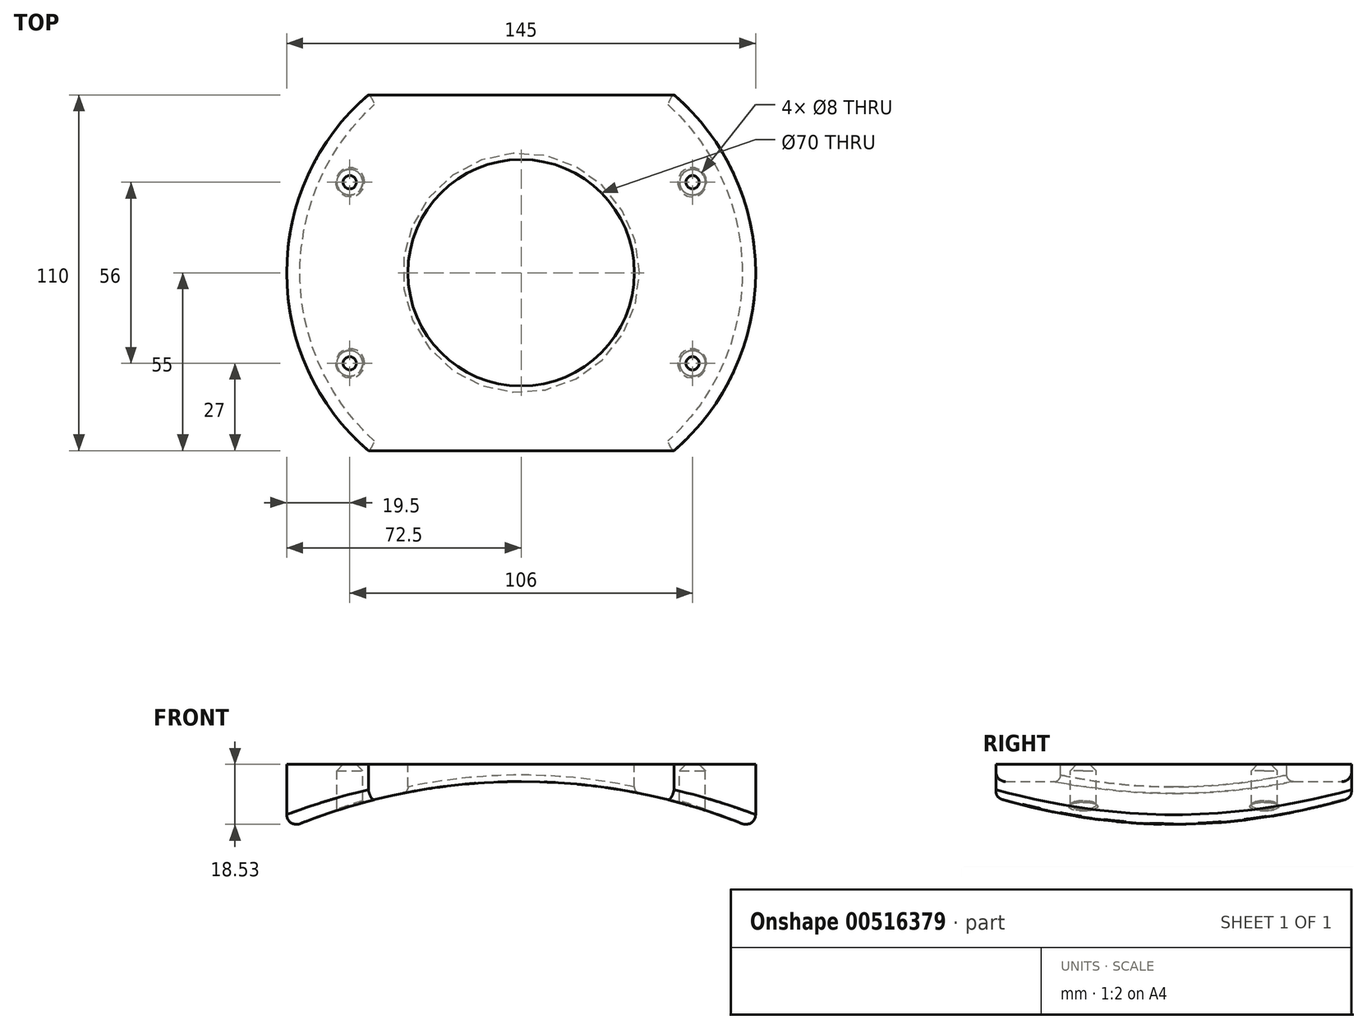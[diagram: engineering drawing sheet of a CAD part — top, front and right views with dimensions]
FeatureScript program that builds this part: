
annotation { "Feature Type Name" : "Feature", "Feature Type Description" : "" }
export const myFeature = defineFeature(function(context is Context, id is Id, definition is map)
    precondition{}
    {
        {
            var Q0;
            Q0=qCreatedBy(makeId("Front.planeOp"),FACE);
            var sketch = newSketch(context, id + "F0", { "sketchPlane" : qUnion([Q0])});
            skLineSegment(sketch, "E0.bottom", {"start": v(0, 0) * mm, "end": v(145, 0) * mm});
            skLineSegment(sketch, "E0.left", {"start": v(0, -20) * mm, "end": v(0, 0) * mm});
            skLineSegment(sketch, "E0.right", {"start": v(145, -20) * mm, "end": v(145, 0) * mm});
            skArc(sketch, "E1", {"start": v(145, -20) * mm, "mid": v(72.5, -5.29) * mm, "end": v(0, -20) * mm});
            skSolve(sketch);
        }
        {
            var Q0;
            Q0 = qSketchRegion(id + "F0", true);
            var Q1;
            Q1 = qSketchRegion(id + "F2", true);
            extrude(context, id + "F1", {"entities" : qUnion([Q0, Q1]), "depth" : 110 * mm, "offsetDistance" : 25 * mm});
        }
        {
            var Q0;
            Q0=makeQuery(id+"F1.opExtrude","SWEPT_FACE",FACE,{"disambiguationData":[OSD([sQuery(id+"F0.wireOp",EDGE,"E0.bottom")])]});
            var sketch = newSketch(context, id + "F2", { "sketchPlane" : qUnion([Q0])});
            skCircle(sketch, "E2", {"center": v(72.5, -55) * mm, "radius": 35 * mm});
            skCircle(sketch, "E3", {"center": v(19.5, -27) * mm, "radius": 4 * mm});
            skCircle(sketch, "E4", {"center": v(125.5, -27) * mm, "radius": 4 * mm});
            skCircle(sketch, "E5", {"center": v(125.5, -83) * mm, "radius": 4 * mm});
            skCircle(sketch, "E6", {"center": v(19.5, -83) * mm, "radius": 4 * mm});
            skCircle(sketch, "E7", {"center": v(19.5, -83) * mm, "radius": 2.05 * mm});
            skCircle(sketch, "E8", {"center": v(19.5, -27) * mm, "radius": 2.05 * mm});
            skCircle(sketch, "E9", {"center": v(125.5, -27) * mm, "radius": 2.05 * mm});
            skCircle(sketch, "E10", {"center": v(125.5, -83) * mm, "radius": 2.05 * mm});
            skLineSegment(sketch, "E11.bottom", {"start": v(119.74, -110) * mm, "end": v(25.26, -110) * mm});
            skLineSegment(sketch, "E11.top", {"start": v(119.74, 0) * mm, "end": v(25.26, 0) * mm});
            skArc(sketch, "E12", {"start": v(119.74, -110) * mm, "mid": v(145, -55) * mm, "end": v(119.74, 0) * mm});
            skArc(sketch, "E13", {"start": v(25.26, 0) * mm, "mid": v(0, -55) * mm, "end": v(25.26, -110) * mm});
            skSolve(sketch);
        }
        {
            var Q0;
            Q0=makeQuery(id+"F2.imprint","IMPRINT",FACE,{"disambiguationData":[TD([[makeQuery(id+"F2.imprint","IMPRINT",EDGE,{"derivedFrom":sQuery(id+"F2.wireOp",EDGE,"E2")}),1.0]])]});
            extrude(context, id + "F3", {"entities" : qUnion([Q0]), "operationType" : NewBodyOperationType.REMOVE, "oppositeDirection" : true, "depth" : 40 * mm, "offsetDistance" : 25 * mm});
        }
        {
            var Q0;
            Q0=makeQuery(id+"F3.boolean.opBoolean","INTERSECT",EDGE,{"derivedFrom":[makeQuery(id+"F1.opExtrude","SWEPT_FACE",FACE,{"disambiguationData":[OSD([sQuery(id+"F0.wireOp",EDGE,"E1")])]}),makeQuery(id+"F3.opExtrude","SWEPT_FACE",FACE,{"disambiguationData":[OSD([sQuery(id+"F2.wireOp",EDGE,"E2")])]})]});
            fillet(context, id + "F4", {"entities" : qUnion([Q0]), "radius" : 2 * mm, "tangentPropagation" : true, "allowEdgeOverflow" : false});
        }
        {
            var Q0;
            Q0=makeQuery(id+"F2.imprint","IMPRINT",FACE,{"disambiguationData":[TD([[makeQuery(id+"F2.imprint","IMPRINT",EDGE,{"derivedFrom":sQuery(id+"F2.wireOp",EDGE,"E6")}),1.0]])]});
            var Q1;
            Q1=makeQuery(id+"F2.imprint","IMPRINT",FACE,{"disambiguationData":[TD([[makeQuery(id+"F2.imprint","IMPRINT",EDGE,{"derivedFrom":sQuery(id+"F2.wireOp",EDGE,"E3")}),1.0]])]});
            var Q2;
            Q2=makeQuery(id+"F2.imprint","IMPRINT",FACE,{"disambiguationData":[TD([[makeQuery(id+"F2.imprint","IMPRINT",EDGE,{"derivedFrom":sQuery(id+"F2.wireOp",EDGE,"E4")}),1.0]])]});
            var Q3;
            Q3=makeQuery(id+"F2.imprint","IMPRINT",FACE,{"disambiguationData":[TD([[makeQuery(id+"F2.imprint","IMPRINT",EDGE,{"derivedFrom":sQuery(id+"F2.wireOp",EDGE,"E5")}),1.0]])]});
            extrude(context, id + "F5", {"entities" : qUnion([Q0, Q1, Q2, Q3]), "operationType" : NewBodyOperationType.REMOVE, "oppositeDirection" : true, "depth" : 40 * mm, "offsetDistance" : 25 * mm});
        }
        {
            var Q0;
            Q0=makeQuery(id+"F5.boolean.opBoolean","INTERSECT",EDGE,{"derivedFrom":[makeQuery(id+"F1.opExtrude","SWEPT_FACE",FACE,{"disambiguationData":[OSD([sQuery(id+"F0.wireOp",EDGE,"E1")])]}),makeQuery(id+"F5.opExtrude","SWEPT_FACE",FACE,{"disambiguationData":[OSD([sQuery(id+"F2.wireOp",EDGE,"E6")])]})]});
            var Q1;
            Q1=makeQuery(id+"F5.boolean.opBoolean","INTERSECT",EDGE,{"derivedFrom":[makeQuery(id+"F1.opExtrude","SWEPT_FACE",FACE,{"disambiguationData":[OSD([sQuery(id+"F0.wireOp",EDGE,"E1")])]}),makeQuery(id+"F5.opExtrude","SWEPT_FACE",FACE,{"disambiguationData":[OSD([sQuery(id+"F2.wireOp",EDGE,"E3")])]})]});
            var Q2;
            Q2=makeQuery(id+"F5.boolean.opBoolean","INTERSECT",EDGE,{"derivedFrom":[makeQuery(id+"F1.opExtrude","SWEPT_FACE",FACE,{"disambiguationData":[OSD([sQuery(id+"F0.wireOp",EDGE,"E1")])]}),makeQuery(id+"F5.opExtrude","SWEPT_FACE",FACE,{"disambiguationData":[OSD([sQuery(id+"F2.wireOp",EDGE,"E4")])]})]});
            var Q3;
            Q3=makeQuery(id+"F5.boolean.opBoolean","INTERSECT",EDGE,{"derivedFrom":[makeQuery(id+"F1.opExtrude","SWEPT_FACE",FACE,{"disambiguationData":[OSD([sQuery(id+"F0.wireOp",EDGE,"E1")])]}),makeQuery(id+"F5.opExtrude","SWEPT_FACE",FACE,{"disambiguationData":[OSD([sQuery(id+"F2.wireOp",EDGE,"E5")])]})]});
            fillet(context, id + "F6", {"entities" : qUnion([Q0, Q1, Q2, Q3]), "radius" : 0.5 * mm, "tangentPropagation" : true, "allowEdgeOverflow" : false});
        }
        {
            var Q0;
            Q0=makeQuery(id+"F2.imprint","IMPRINT",FACE,{"disambiguationData":[TD([[makeQuery(id+"F2.imprint","IMPRINT",EDGE,{"derivedFrom":sQuery(id+"F2.wireOp",EDGE,"E7")}),1.0]])]});
            extrude(context, id + "F7", {"entities" : qUnion([Q0]), "operationType" : NewBodyOperationType.REMOVE, "oppositeDirection" : true, "depth" : 40 * mm, "offsetDistance" : 25 * mm});
        }
        {
            var Q0;
            Q0=makeQuery(id+"F2.imprint","IMPRINT",FACE,{"disambiguationData":[TD([[makeQuery(id+"F2.imprint","IMPRINT",EDGE,{"derivedFrom":sQuery(id+"F2.wireOp",EDGE,"E8")}),1.0]])]});
            extrude(context, id + "F8", {"entities" : qUnion([Q0]), "operationType" : NewBodyOperationType.REMOVE, "oppositeDirection" : true, "depth" : 40 * mm, "offsetDistance" : 25 * mm});
        }
        {
            var Q0;
            Q0=makeQuery(id+"F2.imprint","IMPRINT",FACE,{"disambiguationData":[TD([[makeQuery(id+"F2.imprint","IMPRINT",EDGE,{"derivedFrom":sQuery(id+"F2.wireOp",EDGE,"E9")}),1.0]])]});
            extrude(context, id + "F9", {"entities" : qUnion([Q0]), "operationType" : NewBodyOperationType.REMOVE, "oppositeDirection" : true, "depth" : 40 * mm, "offsetDistance" : 25 * mm});
        }
        {
            var Q0;
            Q0=makeQuery(id+"F2.imprint","IMPRINT",FACE,{"disambiguationData":[TD([[makeQuery(id+"F2.imprint","IMPRINT",EDGE,{"derivedFrom":sQuery(id+"F2.wireOp",EDGE,"E10")}),1.0]])]});
            extrude(context, id + "F10", {"entities" : qUnion([Q0]), "operationType" : NewBodyOperationType.REMOVE, "oppositeDirection" : true, "depth" : 40 * mm, "offsetDistance" : 25 * mm});
        }
        {
            var Q0;
            Q0=makeQuery(id+"F2.imprint","IMPRINT",FACE,{"disambiguationData":[TD([[makeQuery(id+"F2.imprint","IMPRINT",EDGE,{"derivedFrom":sQuery(id+"F2.wireOp",EDGE,"E6")}),1.0]])]});
            var Q1;
            Q1=makeQuery(id+"F2.imprint","IMPRINT",FACE,{"disambiguationData":[TD([[makeQuery(id+"F2.imprint","IMPRINT",EDGE,{"derivedFrom":sQuery(id+"F2.wireOp",EDGE,"E3")}),1.0]])]});
            var Q2;
            Q2=makeQuery(id+"F2.imprint","IMPRINT",FACE,{"disambiguationData":[TD([[makeQuery(id+"F2.imprint","IMPRINT",EDGE,{"derivedFrom":sQuery(id+"F2.wireOp",EDGE,"E4")}),1.0]])]});
            var Q3;
            Q3=makeQuery(id+"F2.imprint","IMPRINT",FACE,{"disambiguationData":[TD([[makeQuery(id+"F2.imprint","IMPRINT",EDGE,{"derivedFrom":sQuery(id+"F2.wireOp",EDGE,"E5")}),1.0]])]});
            extrude(context, id + "F11", {"entities" : qUnion([Q0, Q1, Q2, Q3]), "operationType" : NewBodyOperationType.ADD, "depth" : 0 * mm, "offsetDistance" : 25 * mm, "hasSecondDirection" : true, "secondDirectionOppositeDirection" : true, "secondDirectionDepth" : 3 * mm});
        }
        {
            var Q0;
            Q0=makeQuery(id+"F11.opExtrude","CAP_EDGE",EDGE,{"disambiguationData":[OSD([sQuery(id+"F2.wireOp",EDGE,"E7")])],"isStart":true});
            var Q1;
            Q1=makeQuery(id+"F11.opExtrude","CAP_EDGE",EDGE,{"disambiguationData":[OSD([sQuery(id+"F2.wireOp",EDGE,"E10")])],"isStart":true});
            var Q2;
            Q2=makeQuery(id+"F11.opExtrude","CAP_EDGE",EDGE,{"disambiguationData":[OSD([sQuery(id+"F2.wireOp",EDGE,"E9")])],"isStart":true});
            var Q3;
            Q3=makeQuery(id+"F11.opExtrude","CAP_EDGE",EDGE,{"disambiguationData":[OSD([sQuery(id+"F2.wireOp",EDGE,"E8")])],"isStart":true});
            chamfer(context, id + "F12", {"entities" : qUnion([Q0, Q1, Q2, Q3]), "width" : 3 * mm, "tangentPropagation" : true});
        }
        {
            var Q0;
            {var subQ0=sQuery(id+"F2.wireOp",EDGE,"E12");var subQ1=sQuery(id+"F0.wireOp",EDGE,"E0.bottom");var subQ2=makeQuery(id+"F1.opExtrude","CAP_EDGE",EDGE,{"disambiguationData":[OSD([subQ1])],"isStart":false});var subQ3=makeQuery(id+"F2.imprint","INTERSECT",VERTEX,{"derivedFrom":[subQ2,sQuery(id+"F2.wireOp",EDGE,"E11.bottom"),subQ0]});Q0=makeQuery(id+"F2.imprint","IMPRINT",FACE,{"disambiguationData":[TD([[makeQuery(id+"F2.imprint","IMPRINT",EDGE,{"disambiguationData":[TD([[subQ3,-1.0]])],"derivedFrom":subQ0}),-1.0]])]});}
            var Q1;
            {var subQ0=sQuery(id+"F2.wireOp",EDGE,"E12");var subQ1=sQuery(id+"F0.wireOp",EDGE,"E0.bottom");var subQ2=makeQuery(id+"F1.opExtrude","CAP_EDGE",EDGE,{"disambiguationData":[OSD([subQ1])],"isStart":true});var subQ3=makeQuery(id+"F2.imprint","INTERSECT",VERTEX,{"derivedFrom":[subQ2,sQuery(id+"F2.wireOp",EDGE,"E11.top"),subQ0]});Q1=makeQuery(id+"F2.imprint","IMPRINT",FACE,{"disambiguationData":[TD([[makeQuery(id+"F2.imprint","IMPRINT",EDGE,{"disambiguationData":[TD([[subQ3,1.0]])],"derivedFrom":subQ0}),-1.0]])]});}
            var Q2;
            {var subQ0=sQuery(id+"F2.wireOp",EDGE,"E13");var subQ1=sQuery(id+"F0.wireOp",EDGE,"E0.bottom");var subQ2=makeQuery(id+"F1.opExtrude","CAP_EDGE",EDGE,{"disambiguationData":[OSD([subQ1])],"isStart":true});var subQ3=makeQuery(id+"F2.imprint","INTERSECT",VERTEX,{"derivedFrom":[subQ2,sQuery(id+"F2.wireOp",EDGE,"E11.top"),subQ0]});Q2=makeQuery(id+"F2.imprint","IMPRINT",FACE,{"disambiguationData":[TD([[makeQuery(id+"F2.imprint","IMPRINT",EDGE,{"disambiguationData":[TD([[subQ3,-1.0]])],"derivedFrom":subQ0}),-1.0]])]});}
            var Q3;
            {var subQ0=sQuery(id+"F2.wireOp",EDGE,"E13");var subQ1=sQuery(id+"F0.wireOp",EDGE,"E0.bottom");var subQ2=makeQuery(id+"F1.opExtrude","CAP_EDGE",EDGE,{"disambiguationData":[OSD([subQ1])],"isStart":false});var subQ3=makeQuery(id+"F2.imprint","INTERSECT",VERTEX,{"derivedFrom":[subQ2,sQuery(id+"F2.wireOp",EDGE,"E11.bottom"),subQ0]});Q3=makeQuery(id+"F2.imprint","IMPRINT",FACE,{"disambiguationData":[TD([[makeQuery(id+"F2.imprint","IMPRINT",EDGE,{"disambiguationData":[TD([[subQ3,1.0]])],"derivedFrom":subQ0}),-1.0]])]});}
            extrude(context, id + "F13", {"entities" : qUnion([Q0, Q1, Q2, Q3]), "operationType" : NewBodyOperationType.REMOVE, "depth" : 0 * mm, "offsetDistance" : 25 * mm, "hasSecondDirection" : true, "secondDirectionOppositeDirection" : true, "secondDirectionDepth" : 50 * mm});
        }
        {
            var Q0;
            {var subQ0=sQuery(id+"F2.wireOp",EDGE,"E13");var subQ1=sQuery(id+"F0.wireOp",EDGE,"E0.bottom");var subQ2=sQuery(id+"F0.wireOp",EDGE,"E0.left");var subQ5=sQuery(id+"F0.wireOp",EDGE,"E1");Q0=makeQuery(id+"F13.boolean.opBoolean","INTERSECT",EDGE,{"derivedFrom":[makeQuery(id+"F5.boolean.opBoolean","SPLIT",FACE,{"disambiguationData":[TD([makeQuery(id+"F1.opExtrude","SWEPT_FACE",FACE,{"disambiguationData":[OSD([subQ2])]})])],"derivedFrom":makeQuery(id+"F1.opExtrude","SWEPT_FACE",FACE,{"disambiguationData":[OSD([subQ5])]})}),makeQuery(id+"F13.opExtrude","SWEPT_FACE",FACE,{"disambiguationData":[OSD([subQ0]),TDD([makeQuery(id+"F2.imprint","IMPRINT",EDGE,{"disambiguationData":[TD([[makeQuery(id+"F2.imprint","INTERSECT",VERTEX,{"derivedFrom":[makeQuery(id+"F1.opExtrude","CAP_EDGE",EDGE,{"disambiguationData":[OSD([subQ1])],"isStart":true}),sQuery(id+"F2.wireOp",EDGE,"E11.top"),subQ0]}),-1.0]])],"derivedFrom":subQ0})])]}),makeQuery(id+"F13.opExtrude","SWEPT_FACE",FACE,{"disambiguationData":[OSD([subQ0]),TDD([makeQuery(id+"F2.imprint","IMPRINT",EDGE,{"disambiguationData":[TD([[makeQuery(id+"F2.imprint","INTERSECT",VERTEX,{"derivedFrom":[makeQuery(id+"F1.opExtrude","CAP_EDGE",EDGE,{"disambiguationData":[OSD([subQ1])],"isStart":false}),sQuery(id+"F2.wireOp",EDGE,"E11.bottom"),subQ0]}),1.0]])],"derivedFrom":subQ0})])]})]});}
            var Q1;
            Q1=makeQuery(id+"F1.opExtrude","CAP_EDGE",EDGE,{"disambiguationData":[OSD([sQuery(id+"F0.wireOp",EDGE,"E1")])],"isStart":true});
            var Q2;
            {var subQ0=sQuery(id+"F2.wireOp",EDGE,"E12");var subQ1=sQuery(id+"F0.wireOp",EDGE,"E0.bottom");var subQ4=sQuery(id+"F0.wireOp",EDGE,"E0.left");var subQ5=sQuery(id+"F0.wireOp",EDGE,"E1");Q2=makeQuery(id+"F13.boolean.opBoolean","INTERSECT",EDGE,{"derivedFrom":[makeQuery(id+"F5.boolean.opBoolean","SPLIT",FACE,{"disambiguationData":[TD([makeQuery(id+"F1.opExtrude","SWEPT_FACE",FACE,{"disambiguationData":[OSD([subQ4])]})])],"derivedFrom":makeQuery(id+"F1.opExtrude","SWEPT_FACE",FACE,{"disambiguationData":[OSD([subQ5])]})}),makeQuery(id+"F13.opExtrude","SWEPT_FACE",FACE,{"disambiguationData":[OSD([subQ0]),TDD([makeQuery(id+"F2.imprint","IMPRINT",EDGE,{"disambiguationData":[TD([[makeQuery(id+"F2.imprint","INTERSECT",VERTEX,{"derivedFrom":[makeQuery(id+"F1.opExtrude","CAP_EDGE",EDGE,{"disambiguationData":[OSD([subQ1])],"isStart":false}),sQuery(id+"F2.wireOp",EDGE,"E11.bottom"),subQ0]}),-1.0]])],"derivedFrom":subQ0})])]}),makeQuery(id+"F13.opExtrude","SWEPT_FACE",FACE,{"disambiguationData":[OSD([subQ0]),TDD([makeQuery(id+"F2.imprint","IMPRINT",EDGE,{"disambiguationData":[TD([[makeQuery(id+"F2.imprint","INTERSECT",VERTEX,{"derivedFrom":[makeQuery(id+"F1.opExtrude","CAP_EDGE",EDGE,{"disambiguationData":[OSD([subQ1])],"isStart":true}),sQuery(id+"F2.wireOp",EDGE,"E11.top"),subQ0]}),1.0]])],"derivedFrom":subQ0})])]})]});}
            var Q3;
            Q3=makeQuery(id+"F1.opExtrude","CAP_EDGE",EDGE,{"disambiguationData":[OSD([sQuery(id+"F0.wireOp",EDGE,"E1")])],"isStart":false});
            fillet(context, id + "F14", {"entities" : qUnion([Q0, Q1, Q2, Q3]), "radius" : 3 * mm, "tangentPropagation" : true, "allowEdgeOverflow" : false});
        }
    });
